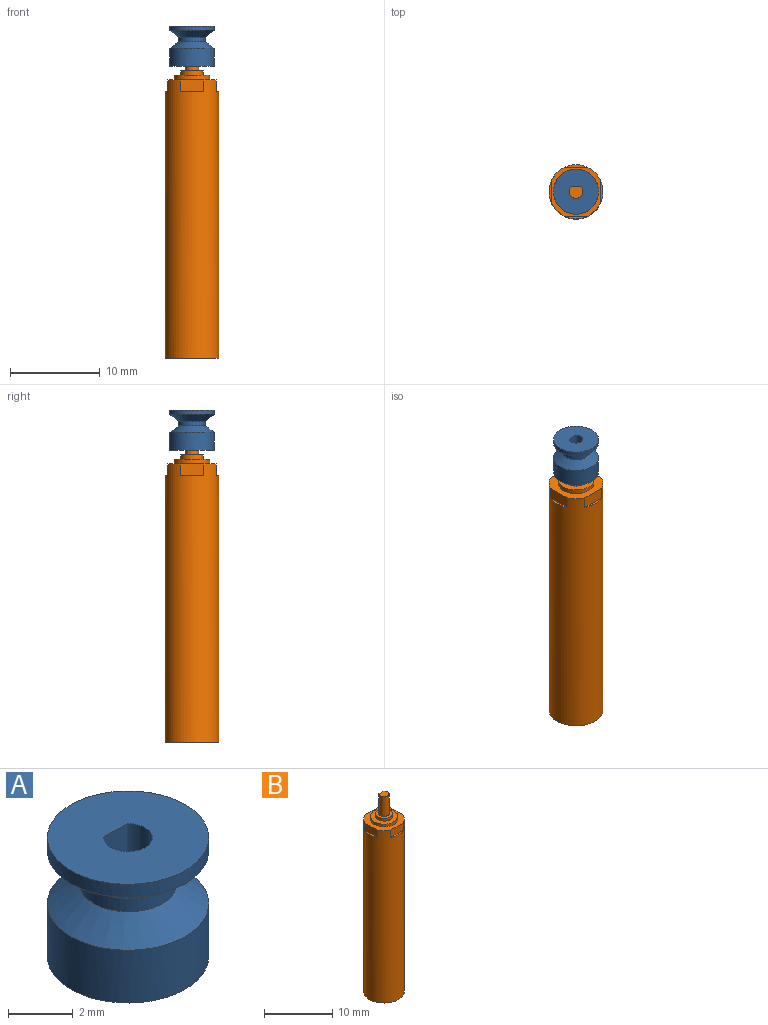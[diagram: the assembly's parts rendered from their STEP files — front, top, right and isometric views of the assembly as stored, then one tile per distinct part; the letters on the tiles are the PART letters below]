
ASSEMBLY  parts=2 mates=1
PART A: 10 faces, bbox 5x5x4.5 mm
  f0: cylinder r=2.5mm len=5mm, axis (0,0,1), area 7.9mm2, adj f6,f9
  f1: cylinder r=2.5mm len=5mm, axis (0,0,1), area 31mm2, adj f4,f5,f8
  f2: cylinder r=0.75mm len=4.5mm, axis (0,0,1), area 16.2mm2, adj f3,f4,f9
  f3: plane 4.5x1.02mm, normal (0,-1,0), area 4.2mm2, adj f2,f4,f5,f9
  f4: plane 5x5mm, normal (0,0,-1), area 18mm2, adj f1,f2,f3
  f5: cylinder r=0.35mm len=1.95mm, axis (0,1,0), area 4.3mm2, adj f1,f3
  f6: cone r=1.5mm half-angle=53.1deg, axis (0,0,1), area 15.7mm2, adj f0,f7
  f7: cylinder r=1.5mm len=3mm, axis (0,0,-1), area 4.7mm2, adj f6,f8
  f8: cone r=1.5mm half-angle=53.1deg, axis (0,0,-1), area 15.7mm2, adj f1,f7
  f9: plane 5x5mm, normal (0,0,1), area 18mm2, adj f0,f2,f3
PART B: 19 faces, bbox 6x6x35.4 mm
  f0: plane 5.4x5.4mm, normal (0,0,1), area 13.6mm2, adj f1,f3,f5,f7,f9,f11
  f1: cylinder r=3mm len=30.9mm, axis (0,0,-1), area 568.4mm2, adj f0,f2,f3,f4,f5,f6,f7,f8
  f2: plane 6x6mm, normal (0,0,-1), area 28.3mm2, adj f1
  f3: plane 2.62x1.3mm, normal (0,-1,0), area 3.4mm2, adj f0,f1,f4
  f4: plane 2.62x0.3mm, normal (0,0,1), area 0.5mm2, adj f1,f3
  f5: plane 2.62x1.3mm, normal (-1,0,0), area 3.4mm2, adj f0,f1,f6
  f6: plane 2.62x0.3mm, normal (0,0,1), area 0.5mm2, adj f1,f5
  f7: plane 2.62x1.3mm, normal (0,1,0), area 3.4mm2, adj f0,f1,f8
  f8: plane 2.62x0.3mm, normal (0,0,1), area 0.5mm2, adj f1,f7
  f9: plane 2.62x1.3mm, normal (1,0,0), area 3.4mm2, adj f0,f1,f10
  f10: plane 2.62x0.3mm, normal (0,0,1), area 0.5mm2, adj f1,f9
  f11: cylinder r=2mm len=4mm, axis (0,0,-1), area 6.3mm2, adj f0,f12
  f12: plane 4x4mm, normal (0,0,1), area 7.7mm2, adj f11,f13
  f13: cylinder r=1.25mm len=2.5mm, axis (0,0,-1), area 3.9mm2, adj f12,f14
  f14: plane 2.5x2.5mm, normal (0,0,1), area 3.1mm2, adj f13,f15
  f15: cylinder r=0.75mm len=3.5mm, axis (0,0,-1), area 13.1mm2, adj f14,f16,f17,f18
  f16: plane 1.5x1.3mm, normal (0,0,1), area 1.6mm2, adj f15,f17
  f17: plane 3x1.02mm, normal (0,1,0), area 3.1mm2, adj f15,f16,f18
  f18: plane 1.02x0.2mm, normal (0,0,1), area 0.1mm2, adj f15,f17
PLACE A at identity
PLACE B at identity
MATE fastened A.f4 <-> B.f18  axis (0,0,-1) through (0,0.55,32.4)mm
